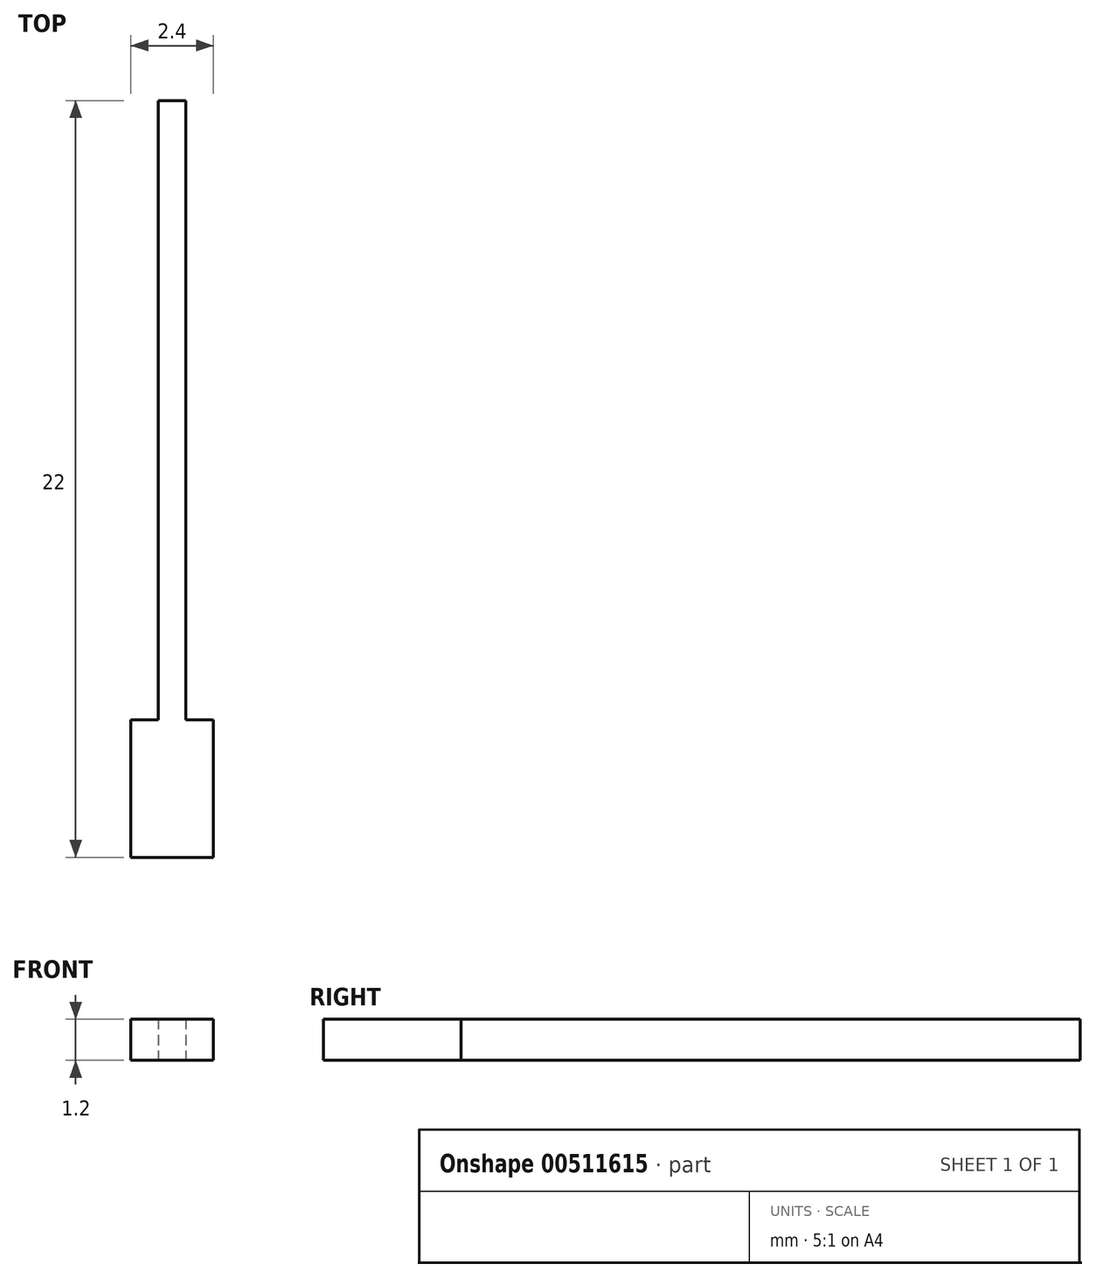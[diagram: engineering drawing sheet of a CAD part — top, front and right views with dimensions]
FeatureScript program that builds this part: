
annotation { "Feature Type Name" : "Feature", "Feature Type Description" : "" }
export const myFeature = defineFeature(function(context is Context, id is Id, definition is map)
    precondition{}
    {
        {
            var Q0;
            Q0=qCreatedBy(makeId("Top.planeOp"),FACE);
            var sketch = newSketch(context, id + "F0", { "sketchPlane" : qUnion([Q0])});
            skLineSegment(sketch, "E0.bottom", {"start": v(0.4, 11) * mm, "end": v(-0.4, 11) * mm});
            skLineSegment(sketch, "E0.top", {"start": v(0.4, -11) * mm, "end": v(-0.4, -11) * mm});
            skLineSegment(sketch, "E0.left", {"start": v(0.4, 11) * mm, "end": v(0.4, -11) * mm});
            skLineSegment(sketch, "E0.right", {"start": v(-0.4, 11) * mm, "end": v(-0.4, -11) * mm});
            skPoint(sketch, "E0.middle", {"position": v(0, 0) * mm});
            skLineSegment(sketch, "E1", {"start": v(0.4, -11) * mm, "end": v(1.2, -11) * mm});
            skLineSegment(sketch, "E2", {"start": v(1.2, -11) * mm, "end": v(1.2, -7) * mm});
            skLineSegment(sketch, "E3", {"start": v(1.2, -7) * mm, "end": v(0.4, -7) * mm});
            skLineSegment(sketch, "E4.MirrorCS", {"start": v(-0.4, -11) * mm, "end": v(-1.2, -11) * mm});
            skLineSegment(sketch, "E5.MirrorCS", {"start": v(-1.2, -11) * mm, "end": v(-1.2, -7) * mm});
            skLineSegment(sketch, "E6.MirrorCS", {"start": v(-1.2, -7) * mm, "end": v(-0.4, -7) * mm});
            skSolve(sketch);
        }
        {
            var Q0;
            Q0 = qSketchRegion(id + "F0", true);
            extrude(context, id + "F1", {"entities" : qUnion([Q0]), "depth" : 1.2 * mm, "offsetDistance" : 25 * mm});
        }
    });
